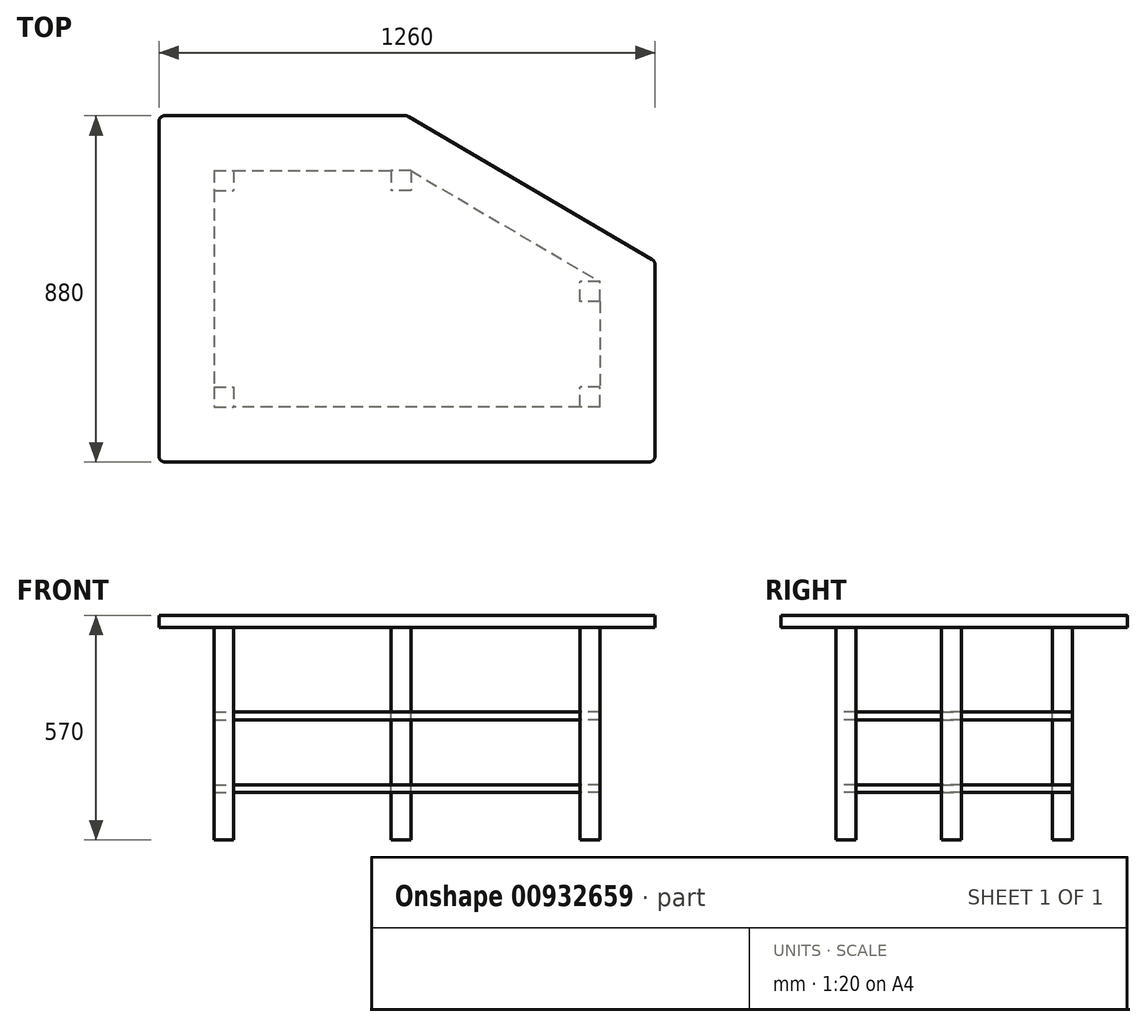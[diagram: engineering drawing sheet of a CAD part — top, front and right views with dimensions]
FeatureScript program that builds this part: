
annotation { "Feature Type Name" : "Feature", "Feature Type Description" : "" }
export const myFeature = defineFeature(function(context is Context, id is Id, definition is map)
    precondition{}
    {
        {
            var Q0;
            Q0=qCreatedBy(makeId("Top.planeOp"),FACE);
            var sketch = newSketch(context, id + "F0", { "sketchPlane" : qUnion([Q0])});
            skLineSegment(sketch, "E0", {"start": v(-85.72, 168.9) * mm, "end": v(525.2, 168.9) * mm});
            skLineSegment(sketch, "E1", {"start": v(532.8, 166.83) * mm, "end": v(1151.88, -196.76) * mm});
            skLineSegment(sketch, "E2", {"start": v(1159.28, -209.7) * mm, "end": v(1159.28, -696.1) * mm});
            skLineSegment(sketch, "E3", {"start": v(1144.28, -711.1) * mm, "end": v(-85.72, -711.1) * mm});
            skLineSegment(sketch, "E4", {"start": v(-100.72, -696.1) * mm, "end": v(-100.72, 153.9) * mm});
            skLineSegment(sketch, "E5.bottom", {"start": v(39.28, 28.9) * mm, "end": v(89.28, 28.9) * mm});
            skLineSegment(sketch, "E5.top", {"start": v(39.28, -21.1) * mm, "end": v(89.28, -21.1) * mm});
            skLineSegment(sketch, "E5.left", {"start": v(39.28, 28.9) * mm, "end": v(39.28, -21.1) * mm});
            skLineSegment(sketch, "E5.right", {"start": v(89.28, 28.9) * mm, "end": v(89.28, -21.1) * mm});
            skLineSegment(sketch, "E6.bottom", {"start": v(39.28, -521.1) * mm, "end": v(89.28, -521.1) * mm});
            skLineSegment(sketch, "E6.top", {"start": v(39.28, -571.1) * mm, "end": v(89.28, -571.1) * mm});
            skLineSegment(sketch, "E6.left", {"start": v(39.28, -521.1) * mm, "end": v(39.28, -571.1) * mm});
            skLineSegment(sketch, "E6.right", {"start": v(89.28, -521.1) * mm, "end": v(89.28, -571.1) * mm});
            skLineSegment(sketch, "E7.bottom", {"start": v(1019.28, -571.1) * mm, "end": v(969.28, -571.1) * mm});
            skLineSegment(sketch, "E7.top", {"start": v(1019.28, -521.1) * mm, "end": v(969.28, -521.1) * mm});
            skLineSegment(sketch, "E7.left", {"start": v(1019.28, -571.1) * mm, "end": v(1019.28, -521.1) * mm});
            skLineSegment(sketch, "E7.right", {"start": v(969.28, -571.1) * mm, "end": v(969.28, -521.1) * mm});
            skLineSegment(sketch, "E8.bottom", {"start": v(1019.28, -303.01) * mm, "end": v(969.28, -303.01) * mm});
            skLineSegment(sketch, "E8.top", {"start": v(1019.28, -253.01) * mm, "end": v(969.28, -253.01) * mm});
            skLineSegment(sketch, "E8.left", {"start": v(1019.28, -303.01) * mm, "end": v(1019.28, -253.01) * mm});
            skLineSegment(sketch, "E8.right", {"start": v(969.28, -303.01) * mm, "end": v(969.28, -253.01) * mm});
            skLineSegment(sketch, "E9.bottom", {"start": v(539.28, 28.9) * mm, "end": v(489.28, 28.9) * mm});
            skLineSegment(sketch, "E9.top", {"start": v(539.28, -21.1) * mm, "end": v(489.28, -21.1) * mm});
            skLineSegment(sketch, "E9.left", {"start": v(539.28, 28.9) * mm, "end": v(539.28, -21.1) * mm});
            skLineSegment(sketch, "E9.right", {"start": v(489.28, 28.9) * mm, "end": v(489.28, -21.1) * mm});
            skLineSegment(sketch, "E10", {"start": v(39.28, -21.1) * mm, "end": v(39.28, -521.1) * mm});
            skLineSegment(sketch, "E11", {"start": v(1019.28, -303.01) * mm, "end": v(1019.28, -521.1) * mm});
            skLineSegment(sketch, "E12", {"start": v(969.28, -571.1) * mm, "end": v(89.28, -571.1) * mm});
            skLineSegment(sketch, "E13", {"start": v(89.28, 28.9) * mm, "end": v(489.28, 28.9) * mm});
            skLineSegment(sketch, "E14", {"start": v(-100.72, 28.9) * mm, "end": v(39.28, 28.9) * mm, "construction": true});
            skLineSegment(sketch, "E15", {"start": v(1019.28, -412.06) * mm, "end": v(1159.28, -412.06) * mm, "construction": true});
            skLineSegment(sketch, "E16", {"start": v(39.28, 28.9) * mm, "end": v(39.28, 168.9) * mm, "construction": true});
            skLineSegment(sketch, "E17", {"start": v(39.28, -711.1) * mm, "end": v(39.28, -571.1) * mm, "construction": true});
            skPoint(sketch, "E18.visualSharp", {"position": v(-100.72, -711.1) * mm});
            skArc(sketch, "E18.filletArc", {"start": v(-100.72, -696.1) * mm, "mid": v(-96.32, -706.71) * mm, "end": v(-85.72, -711.1) * mm});
            skLineSegment(sketch, "E19", {"start": v(1019.28, -253.01) * mm, "end": v(1077.85, -153.28) * mm, "construction": true});
            skLineSegment(sketch, "E20", {"start": v(539.28, 28.9) * mm, "end": v(597.85, 128.62) * mm, "construction": true});
            skPoint(sketch, "E21.visualSharp", {"position": v(1159.28, -711.1) * mm});
            skArc(sketch, "E21.filletArc", {"start": v(1144.28, -711.1) * mm, "mid": v(1154.89, -706.71) * mm, "end": v(1159.28, -696.1) * mm});
            skPoint(sketch, "E22.visualSharp", {"position": v(-100.72, 168.9) * mm});
            skArc(sketch, "E22.filletArc", {"start": v(-85.72, 168.9) * mm, "mid": v(-96.32, 164.5) * mm, "end": v(-100.72, 153.9) * mm});
            skPoint(sketch, "E23.visualSharp", {"position": v(1159.28, -201.1) * mm});
            skArc(sketch, "E23.filletArc", {"start": v(1159.28, -209.7) * mm, "mid": v(1157.3, -202.24) * mm, "end": v(1151.88, -196.76) * mm});
            skPoint(sketch, "E24.visualSharp", {"position": v(529.28, 168.9) * mm});
            skArc(sketch, "E24.filletArc", {"start": v(532.8, 166.83) * mm, "mid": v(529.14, 168.37) * mm, "end": v(525.2, 168.9) * mm});
            skLineSegment(sketch, "E25", {"start": v(539.28, 28.9) * mm, "end": v(1019.28, -253.01) * mm});
            skSolve(sketch);
        }
        {
            var Q0;
            Q0=qCreatedBy(makeId("Front.planeOp"),FACE);
            var sketch = newSketch(context, id + "F1", { "sketchPlane" : qUnion([Q0])});
            skLineSegment(sketch, "E26.bottom", {"start": v(39.28, -4.46) * mm, "end": v(89.28, -4.46) * mm});
            skLineSegment(sketch, "E26.top", {"start": v(39.28, -544.46) * mm, "end": v(89.28, -544.46) * mm});
            skLineSegment(sketch, "E26.left", {"start": v(39.28, -4.46) * mm, "end": v(39.28, -544.46) * mm});
            skLineSegment(sketch, "E26.right", {"start": v(89.28, -4.46) * mm, "end": v(89.28, -544.46) * mm});
            skLineSegment(sketch, "E27.bottom", {"start": v(1019.28, -4.46) * mm, "end": v(969.28, -4.46) * mm});
            skLineSegment(sketch, "E27.top", {"start": v(1019.28, -544.46) * mm, "end": v(969.28, -544.46) * mm});
            skLineSegment(sketch, "E27.left", {"start": v(1019.28, -4.46) * mm, "end": v(1019.28, -544.46) * mm});
            skLineSegment(sketch, "E27.right", {"start": v(969.28, -4.46) * mm, "end": v(969.28, -544.46) * mm});
            skLineSegment(sketch, "E28.bottom", {"start": v(539.28, -4.46) * mm, "end": v(489.28, -4.46) * mm});
            skLineSegment(sketch, "E28.top", {"start": v(539.28, -544.46) * mm, "end": v(489.28, -544.46) * mm});
            skLineSegment(sketch, "E28.left", {"start": v(539.28, -4.46) * mm, "end": v(539.28, -544.46) * mm});
            skLineSegment(sketch, "E28.right", {"start": v(489.28, -4.46) * mm, "end": v(489.28, -544.46) * mm});
            skLineSegment(sketch, "E29", {"start": v(89.28, -4.46) * mm, "end": v(489.28, -4.46) * mm});
            skLineSegment(sketch, "E30", {"start": v(539.28, -4.46) * mm, "end": v(969.28, -4.46) * mm});
            skLineSegment(sketch, "E31", {"start": v(39.28, -4.46) * mm, "end": v(-100.72, -4.46) * mm});
            skLineSegment(sketch, "E32", {"start": v(-100.72, -4.46) * mm, "end": v(-100.72, 25.54) * mm});
            skLineSegment(sketch, "E33", {"start": v(-100.72, 25.54) * mm, "end": v(1159.28, 25.54) * mm});
            skLineSegment(sketch, "E34", {"start": v(1159.28, 25.54) * mm, "end": v(1159.28, -4.46) * mm});
            skLineSegment(sketch, "E35", {"start": v(1159.28, -4.46) * mm, "end": v(1019.28, -4.46) * mm});
            skLineSegment(sketch, "E36.bottom", {"start": v(89.28, -424.46) * mm, "end": v(489.28, -424.46) * mm});
            skLineSegment(sketch, "E36.top", {"start": v(89.28, -219.46) * mm, "end": v(489.28, -219.46) * mm});
            skLineSegment(sketch, "E36.left", {"start": v(89.28, -424.46) * mm, "end": v(89.28, -219.46) * mm});
            skLineSegment(sketch, "E36.right", {"start": v(489.28, -424.46) * mm, "end": v(489.28, -219.46) * mm});
            skLineSegment(sketch, "E37.bottom", {"start": v(539.28, -424.46) * mm, "end": v(969.28, -424.46) * mm});
            skLineSegment(sketch, "E37.top", {"start": v(539.28, -219.46) * mm, "end": v(969.28, -219.46) * mm});
            skLineSegment(sketch, "E37.left", {"start": v(539.28, -424.46) * mm, "end": v(539.28, -219.46) * mm});
            skLineSegment(sketch, "E37.right", {"start": v(969.28, -424.46) * mm, "end": v(969.28, -219.46) * mm});
            skLineSegment(sketch, "E38", {"start": v(489.28, -424.46) * mm, "end": v(539.28, -424.46) * mm});
            skLineSegment(sketch, "E39", {"start": v(489.28, -219.46) * mm, "end": v(539.28, -219.46) * mm});
            skLineSegment(sketch, "E40", {"start": v(89.28, -239.46) * mm, "end": v(489.28, -239.46) * mm});
            skLineSegment(sketch, "E41", {"start": v(489.28, -239.46) * mm, "end": v(539.28, -239.46) * mm});
            skLineSegment(sketch, "E42", {"start": v(539.28, -239.46) * mm, "end": v(969.28, -239.46) * mm});
            skLineSegment(sketch, "E43", {"start": v(89.28, -404.46) * mm, "end": v(489.28, -404.46) * mm});
            skLineSegment(sketch, "E44", {"start": v(122.23, -424.46) * mm, "end": v(122.23, -404.46) * mm, "construction": true});
            skLineSegment(sketch, "E45", {"start": v(122.16, -239.46) * mm, "end": v(122.16, -219.46) * mm, "construction": true});
            skLineSegment(sketch, "E46", {"start": v(489.28, -404.46) * mm, "end": v(539.28, -404.46) * mm});
            skLineSegment(sketch, "E47", {"start": v(539.28, -404.46) * mm, "end": v(969.28, -404.46) * mm});
            skSolve(sketch);
        }
        {
            var Q0;
            Q0=makeQuery(id+"F0.imprint","IMPRINT",FACE,{"disambiguationData":[TD([[makeQuery(id+"F0.imprint","IMPRINT",EDGE,{"derivedFrom":sQuery(id+"F0.wireOp",EDGE,"E6.bottom")}),-1.0]])]});
            var Q1;
            Q1=makeQuery(id+"F0.imprint","IMPRINT",FACE,{"disambiguationData":[TD([[makeQuery(id+"F0.imprint","IMPRINT",EDGE,{"derivedFrom":sQuery(id+"F0.wireOp",EDGE,"E7.bottom")}),-1.0]])]});
            var Q2;
            Q2=makeQuery(id+"F0.imprint","IMPRINT",FACE,{"disambiguationData":[TD([[makeQuery(id+"F0.imprint","IMPRINT",EDGE,{"derivedFrom":sQuery(id+"F0.wireOp",EDGE,"E8.bottom")}),-1.0]])]});
            var Q3;
            Q3=makeQuery(id+"F0.imprint","IMPRINT",FACE,{"disambiguationData":[TD([[makeQuery(id+"F0.imprint","IMPRINT",EDGE,{"derivedFrom":sQuery(id+"F0.wireOp",EDGE,"E9.bottom")}),1.0]])]});
            var Q4;
            Q4=makeQuery(id+"F0.imprint","IMPRINT",FACE,{"disambiguationData":[TD([[makeQuery(id+"F0.imprint","IMPRINT",EDGE,{"derivedFrom":sQuery(id+"F0.wireOp",EDGE,"E5.bottom")}),-1.0]])]});
            var Q5;
            Q5=sQuery(id+"F1.wireOp",VERTEX,"E26.top.start");
            var Q6;
            Q6=sQuery(id+"F1.wireOp",VERTEX,"E26.bottom.start");
            extrude(context, id + "F2", {"entities" : qUnion([Q0, Q1, Q2, Q3, Q4]), "endBound" : BoundingType.UP_TO_VERTEX, "oppositeDirection" : true, "depth" : 25 * mm, "endBoundEntityVertex" : qUnion([Q5]), "offsetDistance" : 25 * mm, "hasSecondDirection" : true, "secondDirectionBound" : SecondDirectionBoundingType.UP_TO_VERTEX, "secondDirectionOppositeDirection" : true, "secondDirectionDepth" : 25 * mm, "secondDirectionBoundEntityVertex" : qUnion([Q6])});
        }
        {
            var Q0;
            Q0=makeQuery(id+"F0.imprint","IMPRINT",FACE,{"disambiguationData":[TD([[makeQuery(id+"F0.imprint","IMPRINT",EDGE,{"derivedFrom":sQuery(id+"F0.wireOp",EDGE,"E6.bottom")}),-1.0]])]});
            var Q1;
            Q1=makeQuery(id+"F0.imprint","IMPRINT",FACE,{"disambiguationData":[TD([[makeQuery(id+"F0.imprint","IMPRINT",EDGE,{"derivedFrom":sQuery(id+"F0.wireOp",EDGE,"E7.bottom")}),-1.0]])]});
            var Q2;
            Q2=makeQuery(id+"F0.imprint","IMPRINT",FACE,{"disambiguationData":[TD([[makeQuery(id+"F0.imprint","IMPRINT",EDGE,{"derivedFrom":sQuery(id+"F0.wireOp",EDGE,"E8.bottom")}),-1.0]])]});
            var Q3;
            Q3=makeQuery(id+"F0.imprint","IMPRINT",FACE,{"disambiguationData":[TD([[makeQuery(id+"F0.imprint","IMPRINT",EDGE,{"derivedFrom":sQuery(id+"F0.wireOp",EDGE,"E9.bottom")}),1.0]])]});
            var Q4;
            Q4=makeQuery(id+"F0.imprint","IMPRINT",FACE,{"disambiguationData":[TD([[makeQuery(id+"F0.imprint","IMPRINT",EDGE,{"derivedFrom":sQuery(id+"F0.wireOp",EDGE,"E5.bottom")}),-1.0]])]});
            var Q5;
            {var subQ1=sQuery(id+"F0.wireOp",EDGE,"E5.top");Q5=makeQuery(id+"F0.imprint","IMPRINT",FACE,{"disambiguationData":[TD([[makeQuery(id+"F0.imprint","IMPRINT",EDGE,{"derivedFrom":subQ1}),-1.0]])]});}
            var Q6;
            Q6=makeQuery(id+"F0.imprint","IMPRINT",FACE,{"disambiguationData":[TD([[makeQuery(id+"F0.imprint","IMPRINT",EDGE,{"derivedFrom":sQuery(id+"F0.wireOp",EDGE,"E0")}),-1.0]])]});
            var Q7;
            {var subQ1=sQuery(id+"F0.wireOp",EDGE,"E6.bottom");Q7=makeQuery(id+"F0.imprint","IMPRINT",FACE,{"disambiguationData":[TD([[makeQuery(id+"F0.imprint","IMPRINT",EDGE,{"derivedFrom":subQ1}),1.0]])]});}
            var Q8;
            {var subQ2=sQuery(id+"F0.wireOp",EDGE,"E8.bottom");Q8=makeQuery(id+"F0.imprint","IMPRINT",FACE,{"disambiguationData":[TD([[makeQuery(id+"F0.imprint","IMPRINT",EDGE,{"derivedFrom":subQ2}),1.0]])]});}
            var Q9;
            Q9=sQuery(id+"F1.wireOp",VERTEX,"E31.end");
            var Q10;
            Q10=sQuery(id+"F1.wireOp",VERTEX,"E32.end");
            extrude(context, id + "F3", {"entities" : qUnion([Q0, Q1, Q2, Q3, Q4, Q5, Q6, Q7, Q8]), "endBound" : BoundingType.UP_TO_VERTEX, "oppositeDirection" : true, "depth" : 25 * mm, "endBoundEntityVertex" : qUnion([Q9]), "offsetDistance" : 25 * mm, "hasSecondDirection" : true, "secondDirectionBound" : SecondDirectionBoundingType.UP_TO_VERTEX, "secondDirectionOppositeDirection" : false, "secondDirectionDepth" : 25 * mm, "secondDirectionBoundEntityVertex" : qUnion([Q10])});
        }
        {
            var Q0;
            {var subQ1=sQuery(id+"F0.wireOp",EDGE,"E5.top");Q0=makeQuery(id+"F0.imprint","IMPRINT",FACE,{"disambiguationData":[TD([[makeQuery(id+"F0.imprint","IMPRINT",EDGE,{"derivedFrom":subQ1}),-1.0]])]});}
            var Q1;
            {var subQ1=sQuery(id+"F0.wireOp",EDGE,"E6.bottom");Q1=makeQuery(id+"F0.imprint","IMPRINT",FACE,{"disambiguationData":[TD([[makeQuery(id+"F0.imprint","IMPRINT",EDGE,{"derivedFrom":subQ1}),1.0]])]});}
            var Q2;
            {var subQ2=sQuery(id+"F0.wireOp",EDGE,"E8.bottom");Q2=makeQuery(id+"F0.imprint","IMPRINT",FACE,{"disambiguationData":[TD([[makeQuery(id+"F0.imprint","IMPRINT",EDGE,{"derivedFrom":subQ2}),1.0]])]});}
            var Q3;
            Q3=sQuery(id+"F1.wireOp",VERTEX,"E44.start");
            var Q4;
            Q4=sQuery(id+"F1.wireOp",VERTEX,"E44.end");
            extrude(context, id + "F4", {"entities" : qUnion([Q0, Q1, Q2]), "endBound" : BoundingType.UP_TO_VERTEX, "oppositeDirection" : true, "depth" : 25 * mm, "endBoundEntityVertex" : qUnion([Q3]), "offsetDistance" : 25 * mm, "hasSecondDirection" : true, "secondDirectionBound" : SecondDirectionBoundingType.UP_TO_VERTEX, "secondDirectionOppositeDirection" : true, "secondDirectionDepth" : 25 * mm, "secondDirectionBoundEntityVertex" : qUnion([Q4])});
        }
        {
            var Q0;
            {var subQ1=sQuery(id+"F0.wireOp",EDGE,"E6.bottom");Q0=makeQuery(id+"F0.imprint","IMPRINT",FACE,{"disambiguationData":[TD([[makeQuery(id+"F0.imprint","IMPRINT",EDGE,{"derivedFrom":subQ1}),1.0]])]});}
            var Q1;
            {var subQ2=sQuery(id+"F0.wireOp",EDGE,"E8.bottom");Q1=makeQuery(id+"F0.imprint","IMPRINT",FACE,{"disambiguationData":[TD([[makeQuery(id+"F0.imprint","IMPRINT",EDGE,{"derivedFrom":subQ2}),1.0]])]});}
            var Q2;
            {var subQ1=sQuery(id+"F0.wireOp",EDGE,"E5.top");Q2=makeQuery(id+"F0.imprint","IMPRINT",FACE,{"disambiguationData":[TD([[makeQuery(id+"F0.imprint","IMPRINT",EDGE,{"derivedFrom":subQ1}),-1.0]])]});}
            var Q3;
            Q3=sQuery(id+"F1.wireOp",VERTEX,"E45.start");
            var Q4;
            Q4=sQuery(id+"F1.wireOp",VERTEX,"E45.end");
            extrude(context, id + "F5", {"entities" : qUnion([Q0, Q1, Q2]), "endBound" : BoundingType.UP_TO_VERTEX, "oppositeDirection" : true, "depth" : 25 * mm, "endBoundEntityVertex" : qUnion([Q3]), "offsetDistance" : 25 * mm, "hasSecondDirection" : true, "secondDirectionBound" : SecondDirectionBoundingType.UP_TO_VERTEX, "secondDirectionOppositeDirection" : true, "secondDirectionDepth" : 25 * mm, "secondDirectionBoundEntityVertex" : qUnion([Q4])});
        }
    });
